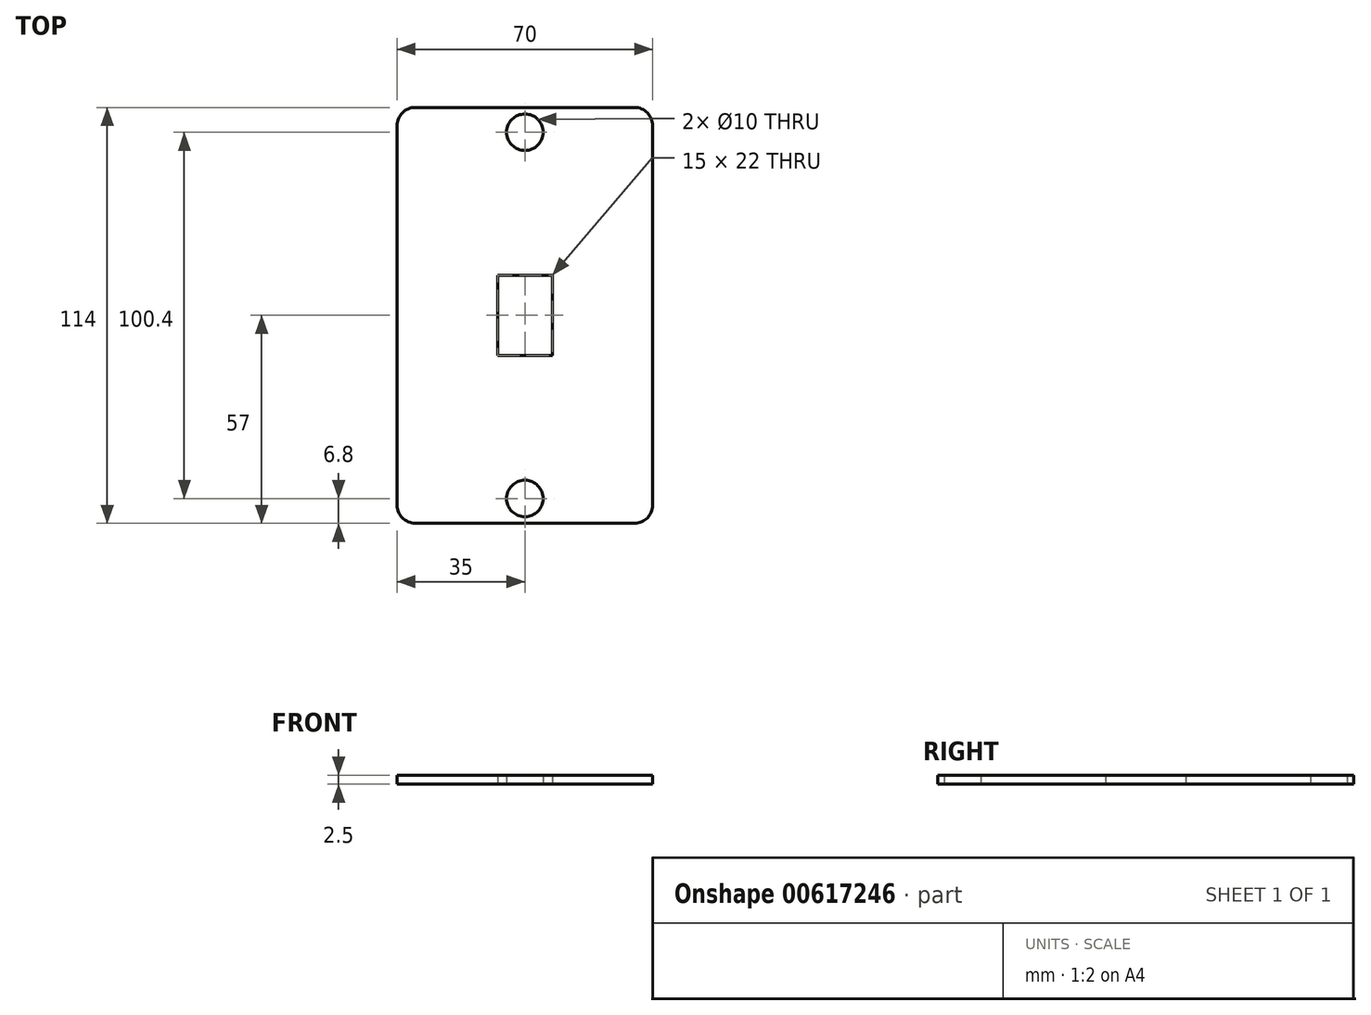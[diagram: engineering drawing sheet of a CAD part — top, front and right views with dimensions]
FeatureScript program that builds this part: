
annotation { "Feature Type Name" : "Feature", "Feature Type Description" : "" }
export const myFeature = defineFeature(function(context is Context, id is Id, definition is map)
    precondition{}
    {
        {
            var Q0;
            Q0=qCreatedBy(makeId("Top.planeOp"),FACE);
            var sketch = newSketch(context, id + "F0", { "sketchPlane" : qUnion([Q0])});
            skLineSegment(sketch, "E0.bottom", {"start": v(-30, 57) * mm, "end": v(30, 57) * mm});
            skLineSegment(sketch, "E0.top", {"start": v(-30, -57) * mm, "end": v(30, -57) * mm});
            skLineSegment(sketch, "E0.left", {"start": v(-35, 52) * mm, "end": v(-35, -52) * mm});
            skLineSegment(sketch, "E0.right", {"start": v(35, 52) * mm, "end": v(35, -52) * mm});
            skPoint(sketch, "E1", {"position": v(0, 57) * mm});
            skPoint(sketch, "E2", {"position": v(35, 0) * mm});
            skCircle(sketch, "E3", {"center": v(0, 50.2) * mm, "radius": 5 * mm});
            skCircle(sketch, "E4.MirrorC", {"center": v(0, -50.2) * mm, "radius": 5 * mm});
            skLineSegment(sketch, "E5.bottom", {"start": v(-7.5, 11) * mm, "end": v(7.5, 11) * mm});
            skLineSegment(sketch, "E5.top", {"start": v(-7.5, -11) * mm, "end": v(7.5, -11) * mm});
            skLineSegment(sketch, "E5.left", {"start": v(-7.5, 11) * mm, "end": v(-7.5, -11) * mm});
            skLineSegment(sketch, "E5.right", {"start": v(7.5, 11) * mm, "end": v(7.5, -11) * mm});
            skPoint(sketch, "E5.middle", {"position": v(0, 0) * mm});
            skPoint(sketch, "E6.visualSharp", {"position": v(-35, 57) * mm});
            skArc(sketch, "E6.filletArc", {"start": v(-30, 57) * mm, "mid": v(-33.54, 55.54) * mm, "end": v(-35, 52) * mm});
            skPoint(sketch, "E7.visualSharp", {"position": v(35, 57) * mm});
            skArc(sketch, "E7.filletArc", {"start": v(35, 52) * mm, "mid": v(33.54, 55.54) * mm, "end": v(30, 57) * mm});
            skPoint(sketch, "E8.visualSharp", {"position": v(35, -57) * mm});
            skArc(sketch, "E8.filletArc", {"start": v(30, -57) * mm, "mid": v(33.54, -55.54) * mm, "end": v(35, -52) * mm});
            skPoint(sketch, "E9.visualSharp", {"position": v(-35, -57) * mm});
            skArc(sketch, "E9.filletArc", {"start": v(-35, -52) * mm, "mid": v(-33.54, -55.54) * mm, "end": v(-30, -57) * mm});
            skSolve(sketch);
        }
        {
            var Q0;
            Q0=makeQuery(id+"F0.imprint","IMPRINT",FACE,{"disambiguationData":[TD([[makeQuery(id+"F0.imprint","IMPRINT",EDGE,{"derivedFrom":sQuery(id+"F0.wireOp",EDGE,"E0.bottom")}),-1.0]])]});
            extrude(context, id + "F1", {"entities" : qUnion([Q0]), "depth" : 2.5 * mm, "offsetDistance" : 25 * mm});
        }
    });
